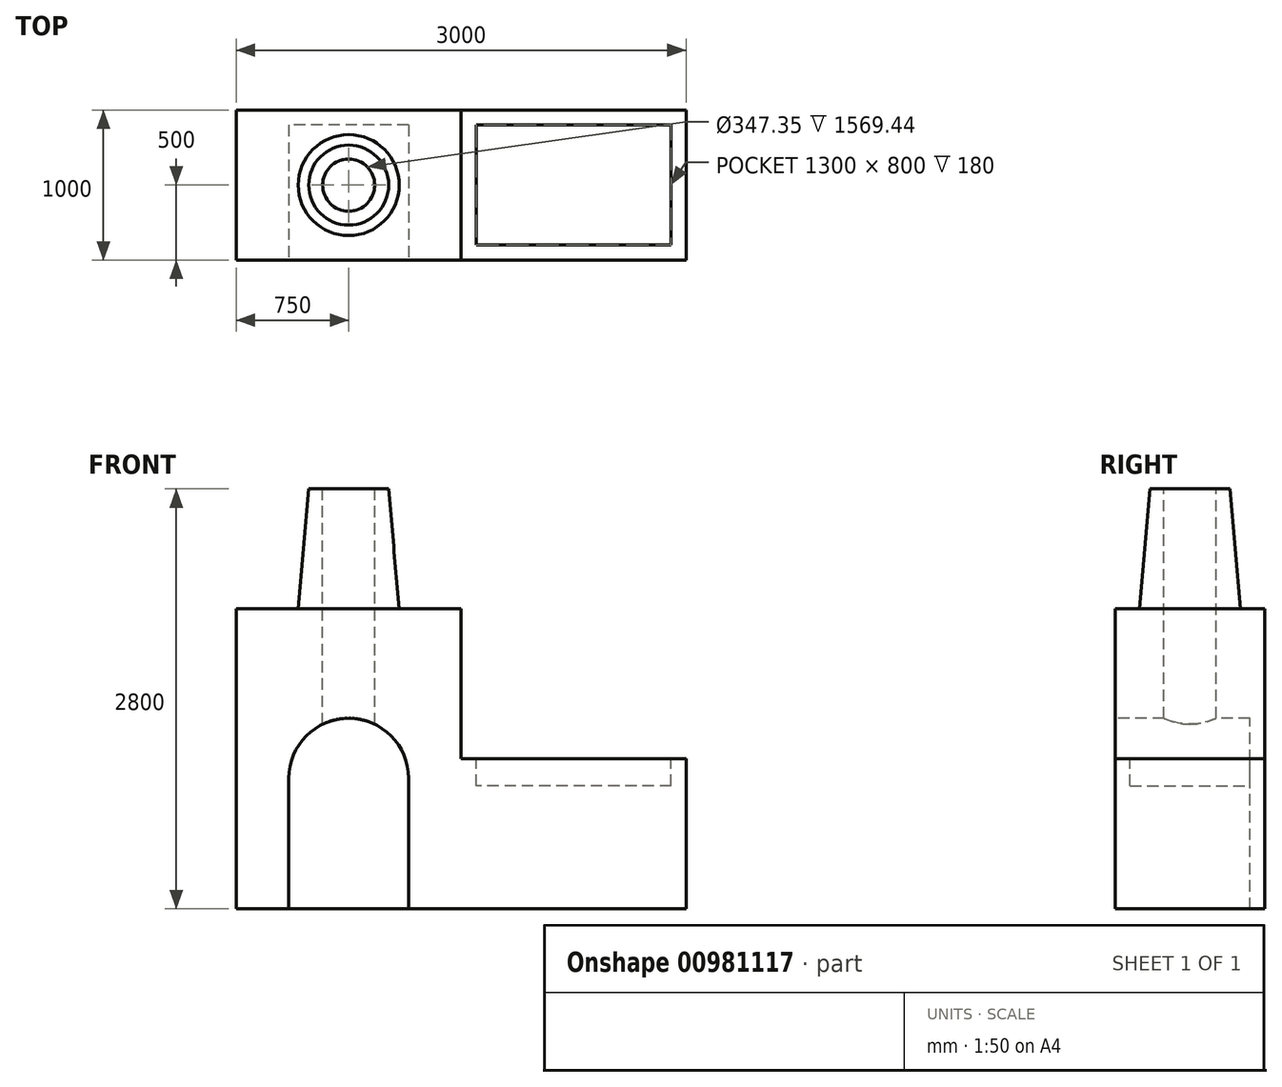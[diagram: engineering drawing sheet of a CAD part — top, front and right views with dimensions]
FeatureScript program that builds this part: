
annotation { "Feature Type Name" : "Feature", "Feature Type Description" : "" }
export const myFeature = defineFeature(function(context is Context, id is Id, definition is map)
    precondition{}
    {
        {
            var Q0;
            Q0=qCreatedBy(makeId("Top.planeOp"),FACE);
            var sketch = newSketch(context, id + "F0", { "sketchPlane" : qUnion([Q0])});
            skLineSegment(sketch, "E0.bottom", {"start": v(1500, -500) * mm, "end": v(-1500, -500) * mm});
            skLineSegment(sketch, "E0.top", {"start": v(1500, 500) * mm, "end": v(-1500, 500) * mm});
            skLineSegment(sketch, "E0.left", {"start": v(1500, -500) * mm, "end": v(1500, 500) * mm});
            skLineSegment(sketch, "E0.right", {"start": v(-1500, -500) * mm, "end": v(-1500, 500) * mm});
            skPoint(sketch, "E0.middle", {"position": v(0, 0) * mm});
            skSolve(sketch);
        }
        {
            var Q0;
            Q0 = qSketchRegion(id + "F0", true);
            extrude(context, id + "F1", {"entities" : qUnion([Q0]), "depth" : 1000 * mm, "offsetDistance" : 25 * mm});
        }
        {
            var Q0;
            Q0=makeQuery(id+"F1.opExtrude","CAP_FACE",FACE,{"disambiguationData":[OSD([sQuery(id+"F0.wireOp",EDGE,"E0.bottom"),sQuery(id+"F0.wireOp",EDGE,"E0.top"),sQuery(id+"F0.wireOp",EDGE,"E0.left"),sQuery(id+"F0.wireOp",EDGE,"E0.right")])],"isStart":false});
            var sketch = newSketch(context, id + "F2", { "sketchPlane" : qUnion([Q0])});
            skLineSegment(sketch, "E1.bottom", {"start": v(-1500, 500) * mm, "end": v(0, 500) * mm});
            skLineSegment(sketch, "E1.top", {"start": v(-1500, -500) * mm, "end": v(0, -500) * mm});
            skLineSegment(sketch, "E1.left", {"start": v(-1500, 500) * mm, "end": v(-1500, -500) * mm});
            skLineSegment(sketch, "E1.right", {"start": v(0, 500) * mm, "end": v(0, -500) * mm});
            skSolve(sketch);
        }
        {
            var Q0;
            Q0 = qSketchRegion(id + "F2", true);
            extrude(context, id + "F3", {"entities" : qUnion([Q0]), "operationType" : NewBodyOperationType.ADD, "depth" : 1000 * mm, "offsetDistance" : 25 * mm});
        }
        {
            var Q0;
            Q0=makeQuery(id+"F3.boolean.opBoolean","MERGE",FACE,{"derivedFrom":[makeQuery(id+"F1.opExtrude","SWEPT_FACE",FACE,{"disambiguationData":[OSD([sQuery(id+"F0.wireOp",EDGE,"E0.bottom")])]}),makeQuery(id+"F3.opExtrude","SWEPT_FACE",FACE,{"disambiguationData":[OSD([sQuery(id+"F2.wireOp",EDGE,"E1.top")])]})]});
            var sketch = newSketch(context, id + "F4", { "sketchPlane" : qUnion([Q0])});
            skLineSegment(sketch, "E2.bottom", {"start": v(-1150, 0) * mm, "end": v(-350, 0) * mm});
            skLineSegment(sketch, "E2.left", {"start": v(-1150, 0) * mm, "end": v(-1150, 870.23) * mm});
            skLineSegment(sketch, "E2.right", {"start": v(-350, 0) * mm, "end": v(-350, 870.23) * mm});
            skArc(sketch, "E3", {"start": v(-1150, 870.23) * mm, "mid": v(-750, 1270.23) * mm, "end": v(-350, 870.23) * mm});
            skLineSegment(sketch, "E4", {"start": v(-750, 2000) * mm, "end": v(-750, 870.23) * mm, "construction": true});
            skSolve(sketch);
        }
        {
            var Q0;
            Q0 = qSketchRegion(id + "F4", true);
            extrude(context, id + "F5", {"entities" : qUnion([Q0]), "operationType" : NewBodyOperationType.REMOVE, "oppositeDirection" : true, "depth" : 900 * mm, "offsetDistance" : 25 * mm});
        }
        {
            var Q0;
            Q0=makeQuery(id+"F1.opExtrude","CAP_FACE",FACE,{"disambiguationData":[OSD([sQuery(id+"F0.wireOp",EDGE,"E0.bottom"),sQuery(id+"F0.wireOp",EDGE,"E0.top"),sQuery(id+"F0.wireOp",EDGE,"E0.left"),sQuery(id+"F0.wireOp",EDGE,"E0.right")])],"isStart":false});
            var sketch = newSketch(context, id + "F6", { "sketchPlane" : qUnion([Q0])});
            skLineSegment(sketch, "E5.0", {"start": v(1400, 400) * mm, "end": v(100, 400) * mm});
            skLineSegment(sketch, "E5.1", {"start": v(1400, -400) * mm, "end": v(1400, 400) * mm});
            skLineSegment(sketch, "E5.2", {"start": v(100, -400) * mm, "end": v(1400, -400) * mm});
            skLineSegment(sketch, "E5.3", {"start": v(100, 400) * mm, "end": v(100, -400) * mm});
            skSolve(sketch);
        }
        {
            var Q0;
            Q0 = qSketchRegion(id + "F6", true);
            extrude(context, id + "F7", {"entities" : qUnion([Q0]), "operationType" : NewBodyOperationType.REMOVE, "oppositeDirection" : true, "depth" : 180 * mm, "offsetDistance" : 25 * mm});
        }
        {
            var Q0;
            Q0=makeQuery(id+"F3.opExtrude","CAP_FACE",FACE,{"disambiguationData":[OSD([sQuery(id+"F2.wireOp",EDGE,"E1.bottom"),sQuery(id+"F2.wireOp",EDGE,"E1.top"),sQuery(id+"F2.wireOp",EDGE,"E1.left"),sQuery(id+"F2.wireOp",EDGE,"E1.right")])],"isStart":false});
            var sketch = newSketch(context, id + "F8", { "sketchPlane" : qUnion([Q0])});
            skLineSegment(sketch, "E6", {"start": v(-750, -500) * mm, "end": v(-750, 500) * mm, "construction": true});
            skCircle(sketch, "E7", {"center": v(-750, 0) * mm, "radius": 336.58 * mm});
            skSolve(sketch);
        }
        {
            var Q0;
            Q0 = qSketchRegion(id + "F8", true);
            extrude(context, id + "F9", {"entities" : qUnion([Q0]), "operationType" : NewBodyOperationType.ADD, "depth" : 800 * mm, "offsetDistance" : 25 * mm, "hasDraft" : true, "draftAngle" : 5 * degree, "draftPullDirection" : true});
        }
        {
            var Q0;
            Q0=makeQuery(id+"F9.opExtrude","CAP_FACE",FACE,{"disambiguationData":[OSD([sQuery(id+"F8.wireOp",EDGE,"E7")])],"isStart":false});
            var sketch = newSketch(context, id + "F10", { "sketchPlane" : qUnion([Q0])});
            skCircle(sketch, "E8", {"center": v(-750, 0) * mm, "radius": 173.67 * mm});
            skSolve(sketch);
        }
        {
            var Q0;
            Q0 = qSketchRegion(id + "F10", true);
            extrude(context, id + "F11", {"entities" : qUnion([Q0]), "operationType" : NewBodyOperationType.REMOVE, "endBound" : BoundingType.THROUGH_ALL, "oppositeDirection" : true, "depth" : 25 * mm, "offsetDistance" : 25 * mm});
        }
    });
